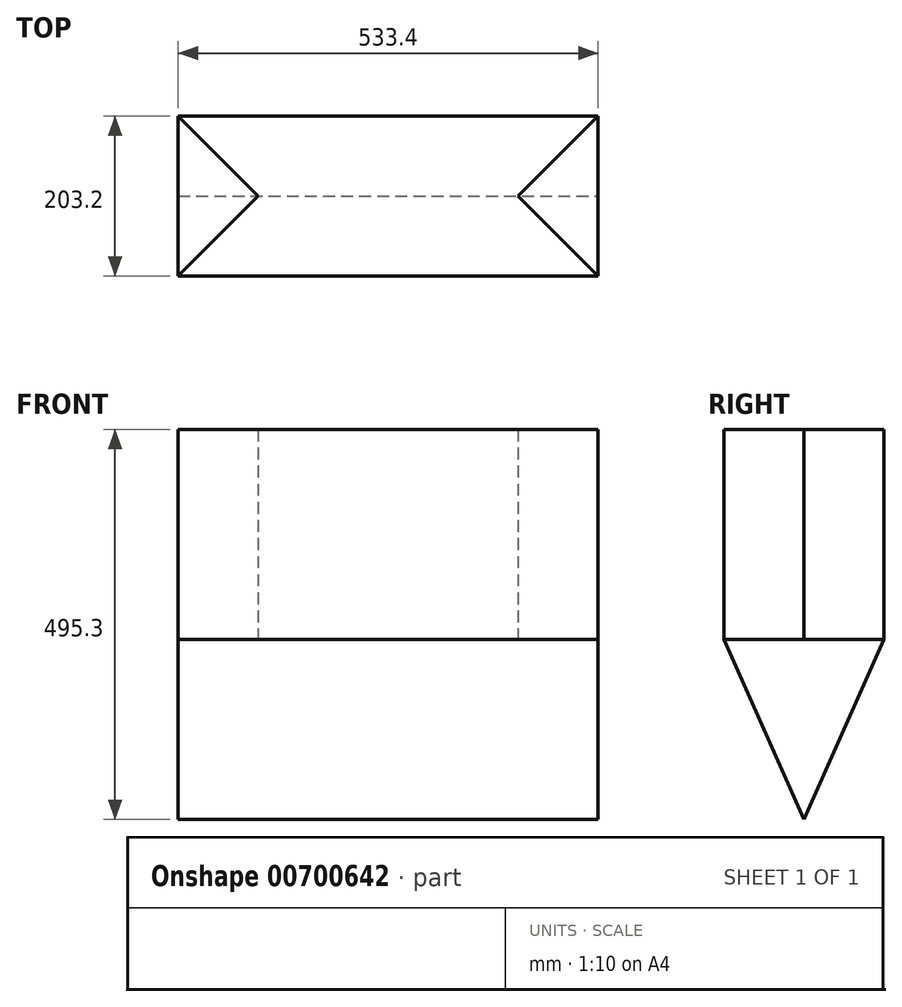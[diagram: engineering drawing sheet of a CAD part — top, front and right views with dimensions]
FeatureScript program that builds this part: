
annotation { "Feature Type Name" : "Feature", "Feature Type Description" : "" }
export const myFeature = defineFeature(function(context is Context, id is Id, definition is map)
    precondition{}
    {
        {
            var Q0;
            Q0=qCreatedBy(makeId("Top.planeOp"),FACE);
            var sketch = newSketch(context, id + "F0", { "sketchPlane" : qUnion([Q0])});
            skLineSegment(sketch, "E0.bottom", {"start": v(-533.4, 101.6) * mm, "end": v(0, 101.6) * mm});
            skLineSegment(sketch, "E0.top", {"start": v(-533.4, -101.6) * mm, "end": v(0, -101.6) * mm});
            skLineSegment(sketch, "E1", {"start": v(-533.4, 101.6) * mm, "end": v(-431.8, 0) * mm});
            skLineSegment(sketch, "E2", {"start": v(-431.8, 0) * mm, "end": v(-533.4, -101.6) * mm});
            skLineSegment(sketch, "E3", {"start": v(0, 101.6) * mm, "end": v(-101.6, 0) * mm});
            skLineSegment(sketch, "E4", {"start": v(-101.6, 0) * mm, "end": v(0, -101.6) * mm});
            skSolve(sketch);
        }
        {
            var Q0;
            Q0 = qSketchRegion(id + "F0", true);
            extrude(context, id + "F1", {"entities" : qUnion([Q0]), "depth" : 266.7 * mm, "offsetDistance" : 25.4 * mm});
        }
        {
            var Q0;
            Q0=qCreatedBy(makeId("Right.planeOp"),FACE);
            var sketch = newSketch(context, id + "F2", { "sketchPlane" : qUnion([Q0])});
            skLineSegment(sketch, "E5", {"start": v(101.6, 0) * mm, "end": v(-101.6, 0) * mm});
            skLineSegment(sketch, "E6", {"start": v(-101.6, 0) * mm, "end": v(0, -228.6) * mm});
            skLineSegment(sketch, "E7", {"start": v(0, -228.6) * mm, "end": v(101.6, 0) * mm});
            skSolve(sketch);
        }
        {
            var Q0;
            Q0=makeQuery(id+"F2.imprint","IMPRINT",FACE,{"disambiguationData":[TD([[makeQuery(id+"F2.imprint","IMPRINT",EDGE,{"derivedFrom":sQuery(id+"F2.wireOp",EDGE,"E5")}),1.0]])]});
            extrude(context, id + "F3", {"entities" : qUnion([Q0]), "operationType" : NewBodyOperationType.ADD, "oppositeDirection" : true, "depth" : 533.4 * mm, "offsetDistance" : 25.4 * mm});
        }
    });
